# Revit family: GC - Assemblaggio Corrente + Rondella + Bullone
name_source: partatom
category: Generic Models
revit_build: Autodesk Revit 2018 (Build: 20170223_1515(x64)
units: mm (PartAtom-declared; Revit-internal decimal feet)

## family parameters
Can host rebar = No
Cut with Voids When Loaded = No
Host = Face
Part Type = Normal
Room Calculation Point = No
Round Connector Dimension = Use Diameter
Shared = No

## types (1)
- GC - Assemblaggio Corrente + Rondella + Bullone
    Corrente _ Diametro Fori = 1.00 cm
    Corrente _ Distanza Fori Centrale = 0.40 cm
    Corrente _ Distanza Fori Laterale = 3.00 cm
    Corrente _ Distanza Fori Laterale 2 = 2.20 cm
    Corrente _ Distanza Piatti = 8.00 cm
    Corrente _ Larghezza = 7.00 cm
    Corrente _ Larghezza Piatto = 4.00 cm
    Corrente _ Lunghezza = 113.20 cm
    Corrente _ Raggio Fori = 0.50 cm
    Corrente _ Spessore = 1.00 cm
    Corrente _ Spessore Piatto = 0.50 cm
    Default Elevation = 121.92 cm

## geometry (parser evidence)
native form markers: Sweep x7
no freeform markers — native parametric forms only
